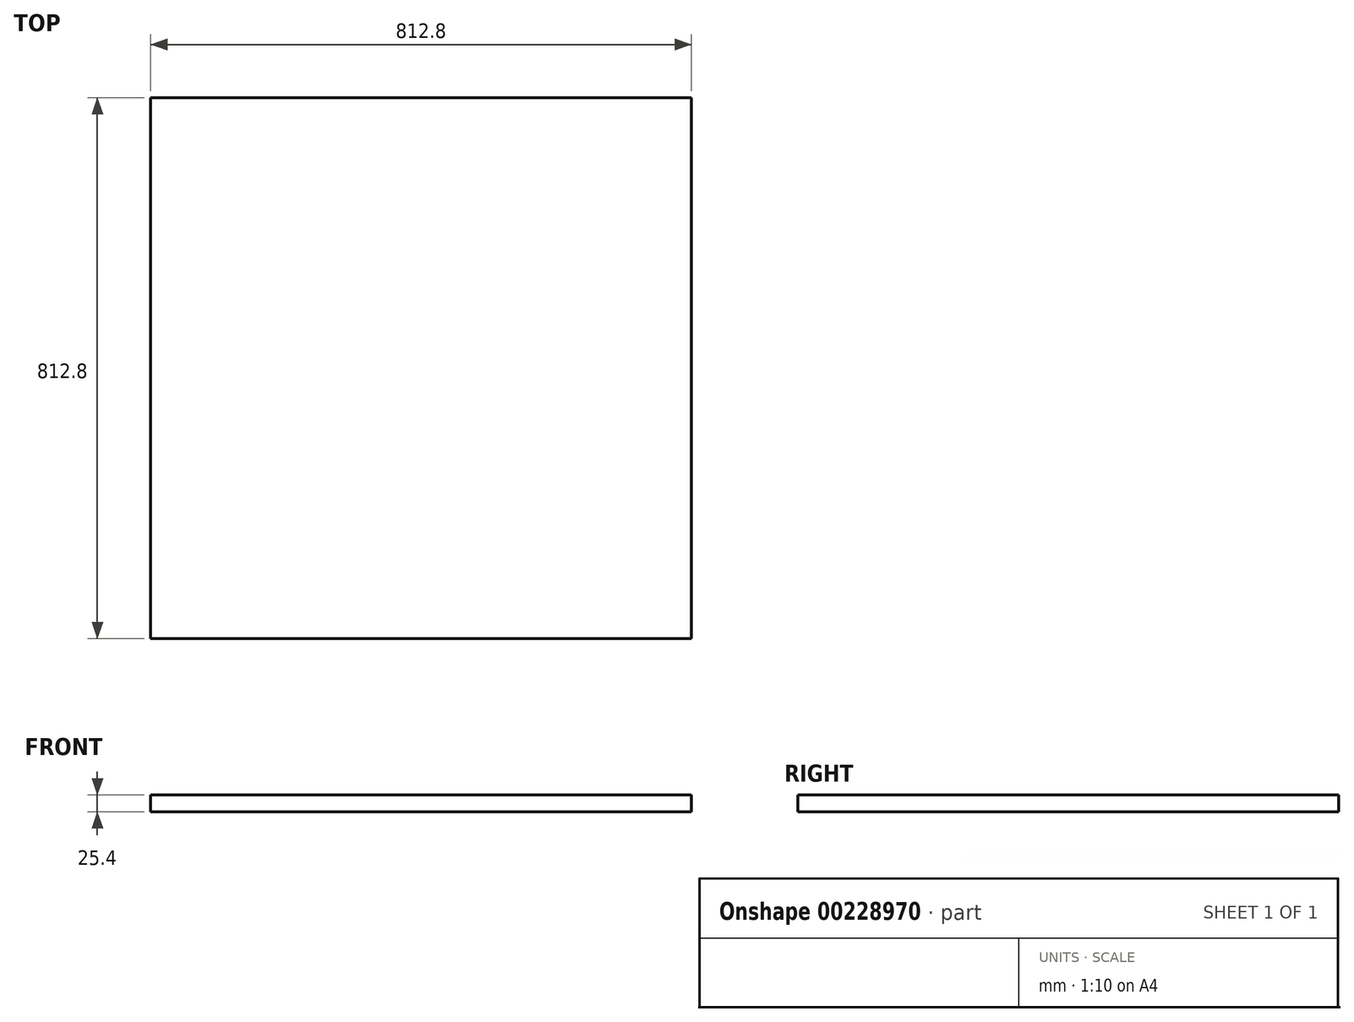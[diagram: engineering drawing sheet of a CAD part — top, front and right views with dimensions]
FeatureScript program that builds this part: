
annotation { "Feature Type Name" : "Feature", "Feature Type Description" : "" }
export const myFeature = defineFeature(function(context is Context, id is Id, definition is map)
    precondition{}
    {
        {
            var Q0;
            Q0=qCreatedBy(makeId("Top.planeOp"),FACE);
            var sketch = newSketch(context, id + "F0", { "sketchPlane" : qUnion([Q0])});
            skLineSegment(sketch, "E0.bottom", {"start": v(0, 0) * mm, "end": v(812.8, 0) * mm});
            skLineSegment(sketch, "E0.top", {"start": v(0, 812.8) * mm, "end": v(812.8, 812.8) * mm});
            skLineSegment(sketch, "E0.left", {"start": v(0, 0) * mm, "end": v(0, 812.8) * mm});
            skLineSegment(sketch, "E0.right", {"start": v(812.8, 0) * mm, "end": v(812.8, 812.8) * mm});
            skSolve(sketch);
        }
        {
            var Q0;
            Q0 = qSketchRegion(id + "F0", true);
            extrude(context, id + "F1", {"entities" : qUnion([Q0]), "depth" : 25.4 * mm});
        }
    });
